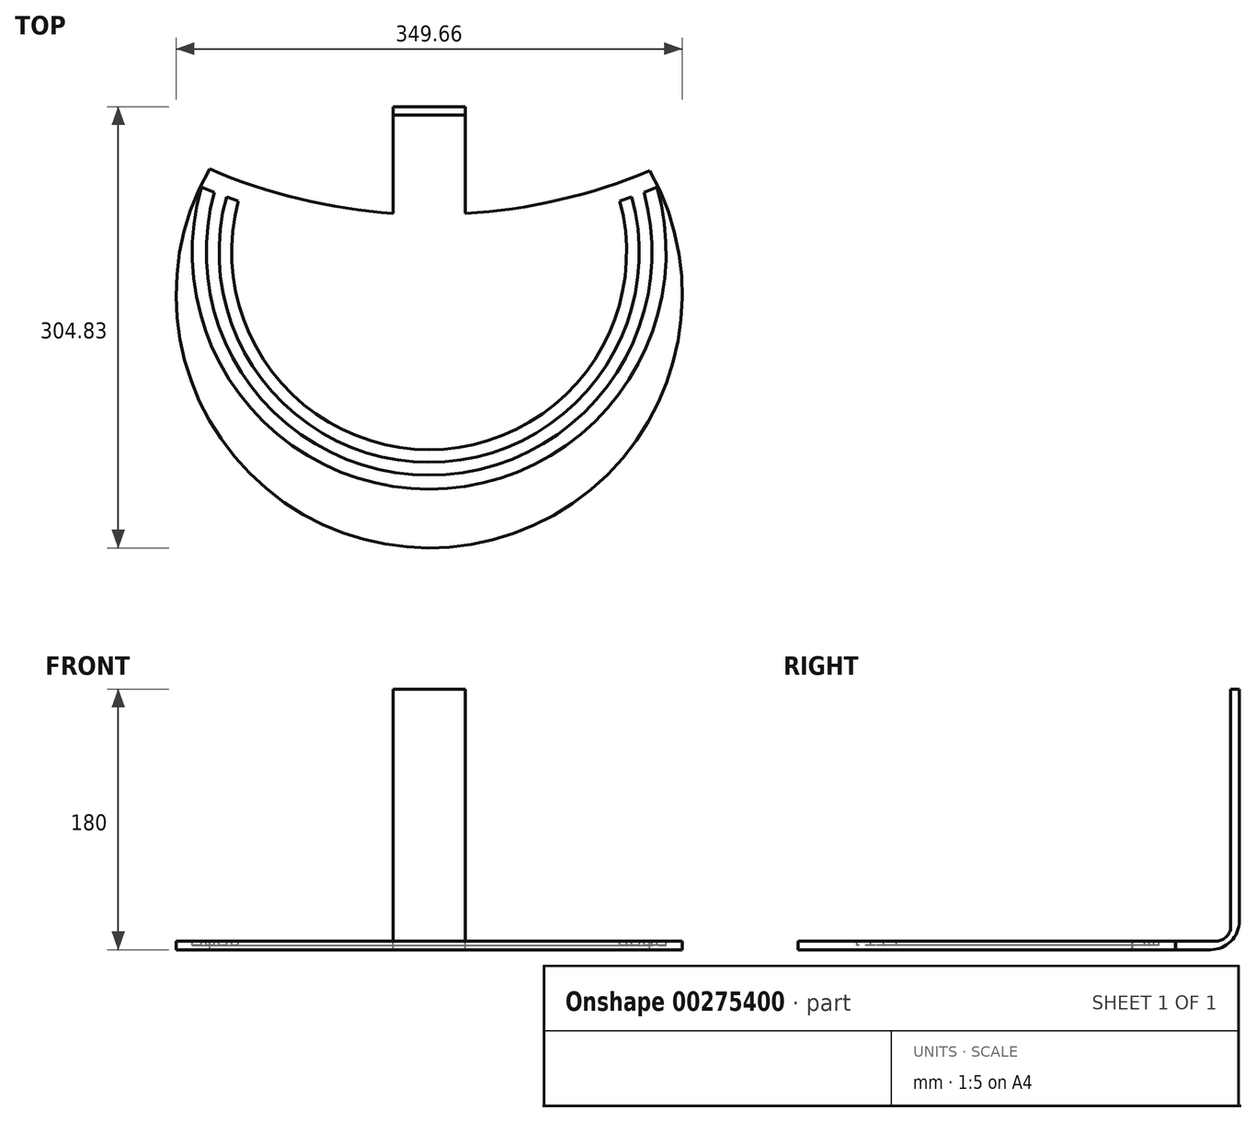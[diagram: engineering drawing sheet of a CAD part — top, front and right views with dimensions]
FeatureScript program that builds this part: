
annotation { "Feature Type Name" : "Feature", "Feature Type Description" : "" }
export const myFeature = defineFeature(function(context is Context, id is Id, definition is map)
    precondition{}
    {
        {
            var Q0;
            Q0=qCreatedBy(makeId("Front.planeOp"),FACE);
            var sketch = newSketch(context, id + "F0", { "sketchPlane" : qUnion([Q0])});
            skLineSegment(sketch, "E0.bottom", {"start": v(-30, 30) * mm, "end": v(20, 30) * mm});
            skLineSegment(sketch, "E0.top", {"start": v(-30, -70) * mm, "end": v(20, -70) * mm});
            skLineSegment(sketch, "E0.left", {"start": v(-30, 30) * mm, "end": v(-30, -70) * mm});
            skLineSegment(sketch, "E0.right", {"start": v(20, 30) * mm, "end": v(20, -70) * mm});
            skLineSegment(sketch, "E1.top", {"start": v(-30, -150) * mm, "end": v(20, -150) * mm});
            skLineSegment(sketch, "E1.left", {"start": v(-30, -70) * mm, "end": v(-30, -150) * mm});
            skLineSegment(sketch, "E1.right", {"start": v(20, -70) * mm, "end": v(20, -150) * mm});
            skLineSegment(sketch, "E2.top", {"start": v(-30, -144) * mm, "end": v(20, -144) * mm});
            skLineSegment(sketch, "E2.left", {"start": v(-30, -150) * mm, "end": v(-30, -144) * mm});
            skLineSegment(sketch, "E2.right", {"start": v(20, -150) * mm, "end": v(20, -144) * mm});
            skSolve(sketch);
        }
        {
            var Q0;
            Q0=makeQuery(id+"F0.imprint","IMPRINT",FACE,{"disambiguationData":[TD([[makeQuery(id+"F0.imprint","IMPRINT",EDGE,{"derivedFrom":sQuery(id+"F0.wireOp",EDGE,"E1.top")}),1.0]])]});
            var sketch = newSketch(context, id + "F1", { "sketchPlane" : qUnion([Q0])});
            skSolve(sketch);
        }
        {
            var Q0;
            Q0=qSketchRegion(id+"F1",true);
            var Q1;
            Q1=makeQuery(id+"F0.imprint","IMPRINT",FACE,{"disambiguationData":[TD([[makeQuery(id+"F0.imprint","IMPRINT",EDGE,{"derivedFrom":sQuery(id+"F0.wireOp",EDGE,"E1.top")}),1.0]])]});
            extrude(context, id + "F2", {"entities" : qUnion([Q0, Q1]), "depth" : 130 * mm});
        }
        {
            var Q0;
            Q0=qSketchRegion(id+"F0",true);
            extrude(context, id + "F3", {"entities" : qUnion([Q0]), "operationType" : NewBodyOperationType.ADD, "depth" : 6 * mm, "offsetDistance" : 25 * mm});
        }
        {
            var Q0;
            Q0=makeQuery(id+"F2.opExtrude","CAP_EDGE",EDGE,{"disambiguationData":[OSD([sQuery(id+"F0.wireOp",EDGE,"E1.top")])],"isStart":true});
            fillet(context, id + "F4", {"entities" : qUnion([Q0]), "radius" : 20 * mm, "tangentPropagation" : true, "allowEdgeOverflow" : false});
        }
        {
            var Q0;
            Q0=makeQuery(id+"F3.boolean.opBoolean","INTERSECT",EDGE,{"derivedFrom":[makeQuery(id+"F2.opExtrude","SWEPT_FACE",FACE,{"disambiguationData":[OSD([sQuery(id+"F0.wireOp",EDGE,"E2.top")])]}),makeQuery(id+"F3.opExtrude","CAP_FACE",FACE,{"disambiguationData":[OSD([sQuery(id+"F0.wireOp",EDGE,"E0.bottom"),sQuery(id+"F0.wireOp",EDGE,"E0.left"),sQuery(id+"F0.wireOp",EDGE,"E0.right"),sQuery(id+"F0.wireOp",EDGE,"E1.left"),sQuery(id+"F0.wireOp",EDGE,"E1.right"),sQuery(id+"F0.wireOp",EDGE,"E1.top"),sQuery(id+"F0.wireOp",EDGE,"E2.left"),sQuery(id+"F0.wireOp",EDGE,"E2.right")])],"isStart":false})]});
            fillet(context, id + "F5", {"entities" : qUnion([Q0]), "radius" : 10 * mm, "tangentPropagation" : true, "allowEdgeOverflow" : false});
        }
        {
            var Q0;
            Q0=makeQuery(id+"F2.opExtrude","SWEPT_FACE",FACE,{"disambiguationData":[OSD([sQuery(id+"F0.wireOp",EDGE,"E2.top")])]});
            var sketch = newSketch(context, id + "F6", { "sketchPlane" : qUnion([Q0])});
            skArc(sketch, "E3", {"start": v(-156.74, -43.16) * mm, "mid": v(-5.6, -304.83) * mm, "end": v(147.34, -44.22) * mm});
            skArc(sketch, "E4", {"start": v(-156.74, -43.16) * mm, "mid": v(-4.8, -74.61) * mm, "end": v(147.34, -44.22) * mm});
            skSolve(sketch);
        }
        {
            var Q0;
            {var subQ3=sQuery(id+"F6.wireOp",EDGE,"E3");Q0=makeQuery(id+"F6.imprint","IMPRINT",FACE,{"disambiguationData":[TD([[makeQuery(id+"F6.imprint","IMPRINT",EDGE,{"derivedFrom":subQ3}),1.0]])]});}
            extrude(context, id + "F7", {"entities" : qUnion([Q0]), "operationType" : NewBodyOperationType.ADD, "oppositeDirection" : true, "depth" : 6 * mm});
        }
        {
            var Q0;
            {var subQ0=sQuery(id+"F0.wireOp",EDGE,"E2.top");Q0=makeQuery(id+"F7.boolean.opBoolean","MERGE",FACE,{"derivedFrom":[makeQuery(id+"F2.opExtrude","SWEPT_FACE",FACE,{"disambiguationData":[OSD([subQ0])]}),makeQuery(id+"F7.opExtrude","CAP_FACE",FACE,{"disambiguationData":[OSD([sQuery(id+"F0.wireOp",EDGE,"E1.left"),sQuery(id+"F0.wireOp",EDGE,"E1.right"),subQ0,sQuery(id+"F0.wireOp",EDGE,"E2.left"),sQuery(id+"F0.wireOp",EDGE,"E2.right"),sQuery(id+"F6.wireOp",EDGE,"E3"),sQuery(id+"F6.wireOp",EDGE,"E4")])],"isStart":true})]});}
            var sketch = newSketch(context, id + "F8", { "sketchPlane" : qUnion([Q0])});
            skArc(sketch, "E5", {"start": v(-153.3, -59.08) * mm, "mid": v(-127.68, -193.64) * mm, "end": v(-5, -254.55) * mm});
            skPoint(sketch, "E5.centerSnap0", {"position": v(-5, -16) * mm});
            skArc(sketch, "E6", {"start": v(-162.38, -55.63) * mm, "mid": v(-135.65, -199.13) * mm, "end": v(-5, -264.22) * mm});
            skArc(sketch, "E7", {"start": v(-145, -62.24) * mm, "mid": v(-120.38, -188.6) * mm, "end": v(-5, -245.7) * mm});
            skArc(sketch, "E8", {"start": v(-136.76, -65.37) * mm, "mid": v(-113.16, -183.62) * mm, "end": v(-5, -236.93) * mm});
            skLineSegment(sketch, "E9", {"start": v(-162.38, -55.63) * mm, "end": v(-153.3, -59.08) * mm});
            skLineSegment(sketch, "E10", {"start": v(-5, -100.56) * mm, "end": v(-5, -286.78) * mm, "construction": true});
            skLineSegment(sketch, "E11", {"start": v(-5, -286.78) * mm, "end": v(-5, -100.56) * mm, "construction": true});
            skLineSegment(sketch, "E12", {"start": v(0, 71.96) * mm, "end": v(-5, 73.8) * mm, "construction": true});
            skLineSegment(sketch, "E13", {"start": v(-5, 73.8) * mm, "end": v(-5, -100.56) * mm, "construction": true});
            skLineSegment(sketch, "E14.trimOffspring", {"start": v(-145, -62.24) * mm, "end": v(-136.76, -65.37) * mm});
            skLineSegment(sketch, "E15.MirrorCS", {"start": v(152.38, -55.63) * mm, "end": v(143.3, -59.08) * mm});
            skLineSegment(sketch, "E16.MirrorCS", {"start": v(135, -62.24) * mm, "end": v(126.76, -65.37) * mm});
            skArc(sketch, "E17.MirrorCS", {"start": v(126.76, -65.37) * mm, "mid": v(103.16, -183.62) * mm, "end": v(-5, -236.93) * mm});
            skArc(sketch, "E18.MirrorCS", {"start": v(135, -62.24) * mm, "mid": v(110.38, -188.6) * mm, "end": v(-5, -245.7) * mm});
            skArc(sketch, "E19.MirrorCS", {"start": v(152.38, -55.63) * mm, "mid": v(125.65, -199.13) * mm, "end": v(-5, -264.22) * mm});
            skArc(sketch, "E20.MirrorCS", {"start": v(143.3, -59.08) * mm, "mid": v(117.68, -193.64) * mm, "end": v(-5, -254.55) * mm});
            skSolve(sketch);
        }
        {
            var Q0;
            Q0=makeQuery(id+"F8.imprint","IMPRINT",FACE,{"disambiguationData":[TD([[makeQuery(id+"F8.imprint","IMPRINT",EDGE,{"derivedFrom":sQuery(id+"F8.wireOp",EDGE,"E5")}),-1.0]])]});
            var Q1;
            Q1=makeQuery(id+"F8.imprint","IMPRINT",FACE,{"disambiguationData":[TD([[makeQuery(id+"F8.imprint","IMPRINT",EDGE,{"derivedFrom":sQuery(id+"F8.wireOp",EDGE,"E7")}),1.0]])]});
            extrude(context, id + "F9", {"entities" : qUnion([Q0, Q1]), "operationType" : NewBodyOperationType.REMOVE, "oppositeDirection" : true, "depth" : 3 * mm});
        }
    });
